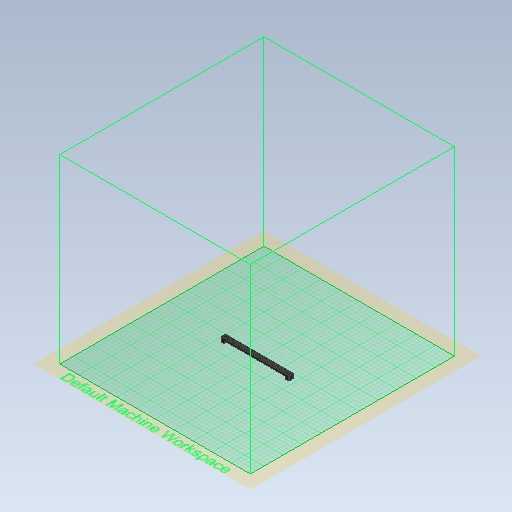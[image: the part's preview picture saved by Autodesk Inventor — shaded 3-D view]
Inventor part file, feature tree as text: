
AUTODESK INVENTOR PART (.ipt)
format: ipt  version: 2021 (Build 250183000, 183)  size: 846,336 bytes
history: native  units: mm
features: extrude x14, sketch x14, chamfer x11, thicken_offset x8, fillet x4, plane x3, mirror x3, projected_geometry x3
ambient origin geometry x8: Origin, YZ Plane, XZ Plane, XY Plane, X Axis, Y Axis, Z Axis, Center Point
bodies: Solid1 (feature_tree), Solid2 (feature_tree)
feature tree (60):
  extrude  "Extrusion1"  Depth=10.0mm
  extrude  "Extrusion2"  Depth=10.0mm
  extrude  "Extrusion3"  Depth=5.0mm
  sketch  "Sketch4"  dims[d10=0.0mm d11=0.0mm d12=1.6mm]
  plane  "Work Plane1"
  extrude  "Extrusion5"  Depth=1.6mm
  extrude  "Extrusion6"  Depth=5.6mm
  sketch  "Sketch6"  dims[d21=2.0mm d22=3.75mm d23=0.0mm d25=5.3mm d27=0.0mm d28=0.0mm]
  plane  "Work Plane2"
  extrude  "Extrusion7"  Depth=5.3mm
  mirror  "Mirror1"
  chamfer  "Chamfer3"  [1 undecoded]
  chamfer  "Chamfer5"  Distance=3.75mm
  chamfer  "Chamfer6"  Distance=0.5mm Angle=45.0deg
  extrude  "Extrusion8"  Depth=70.0mm
  chamfer  "Chamfer7"  Distance=2.0mm Angle=45.0deg
  chamfer  "Chamfer8"  [1 undecoded]
  thicken_offset  "Thicken1"
  thicken_offset  "Thicken2"
  chamfer  "Chamfer9"  Distance=0.5mm Angle=45.0deg
  extrude  "Extrusion9"  Depth=2.0mm
  chamfer  "Chamfer11"  Distance=0.2mm
  extrude  "Extrusion10"  Depth=2.0mm
  extrude  "Extrusion11"  Depth=0.5mm TaperAngle=45.0deg
  mirror  "Mirror2"
  extrude  "Extrusion12"  Depth=6.5mm
  sketch  "Sketch13"  dims[d45=0.5mm d46=2.0mm d47=45.0deg d48=70.0mm d49=1.9mm d50=2.0mm d51=45.0deg d52=0.0mm d53=0.0mm d54=0.5mm d55=2.0mm d56=45.0deg]
  mirror  "Mirror3"
  extrude  "Extrusion13"  Depth=3.0mm
  extrude  "Extrusion14"  Depth=5.0mm
  fillet  "Fillet2"  Radius=2.5mm
  chamfer  "Chamfer14"  Distance=0.5mm Angle=45.0deg
  chamfer  "Chamfer15"  [1 undecoded]
  fillet  "Fillet4"  Radius=10.0mm
  thicken_offset  "Thicken3"
  fillet  "Fillet5"  Radius=3.0mm
  thicken_offset  "Thicken4"
  thicken_offset  "Thicken5"
  fillet  "Fillet6"  [1 undecoded]
  extrude  "Extrusion15"  Depth=2.0mm
  chamfer  "Chamfer16"  Distance=3.0mm
  thicken_offset  "Thicken6"
  thicken_offset  "Thicken7"
  thicken_offset  "Thicken8"
  chamfer  "Chamfer17"  Distance=1.5mm
  sketch  "Sketch1"  dims[d0=150.0mm d1=10.0mm]
  sketch  "Sketch2"  dims[d2=10.0mm d3=0.0mm d7=67.5mm]
  sketch  "Sketch3"  dims[d8=135.0mm d9=5.0mm]
  sketch  "Sketch5"  dims[d13=2.0mm d14=0.0mm d18=5.6mm]
  projected_geometry  "Projected Loop1"
  plane  "Work Plane3"
  sketch  "Sketch7"  dims[d29=-2.0mm d30=3.75mm d31=0.0mm]
  sketch  "Sketch8"  dims[d32=2.0mm]
  sketch  "Sketch9"  dims[d33=3.0mm]
  sketch  "Sketch10"  dims[d34=2.8mm]
  projected_geometry  "Projected Loop2"
  projected_geometry  "Projected Loop3"
  sketch  "Sketch12"  dims[d35=5.6mm d39=0.5mm d40=2.0mm d41=45.0deg]
  sketch  "Sketch14"  dims[d57=0.5mm d58=2.0mm d59=45.0deg d60=0.2mm]
  sketch  "Sketch18"  dims[d61=0.2mm d62=0.2mm d63=0.2mm d64=0.5mm d65=2.0mm d66=45.0deg d70=6.5mm d71=3.0mm d72=5.0mm d73=2.5mm d74=0.0mm d75=0.5mm d76=2.0mm d77=45.0deg d78=0.0mm d79=0.0mm d80=10.0mm d81=0.0mm d88=3.0mm d89=0.0mm d90=0.0mm d91=0.0mm d93=0.56mm d94=3.0mm d95=0.0mm d96=1.5mm d97=0.5mm d98=2.0mm d99=45.0deg d101=0.5mm d102=2.0mm d103=45.0deg d104=1.5mm d105=0.25mm d106=0.25mm d107=0.5mm d108=2.116859mm d109=0.25mm d110=0.25mm d111=0.25mm d112=0.25mm d113=1.5mm d114=3.1mm d115=0.35mm d116=1.55mm d117=3.0mm d118=0.0mm d119=0.5mm d120=2.0mm d121=45.0deg d122=0.25mm d123=0.25mm d124=0.25mm d125=0.25mm d126=1.0mm d127=1.0mm d128=0.5mm d129=2.0mm d130=45.0deg]
note: 4 required parameter values undecoded (feature->parameter linkage not recoverable at this tier; creation-order binding heuristic only, values carry confidence <= 0.55)
